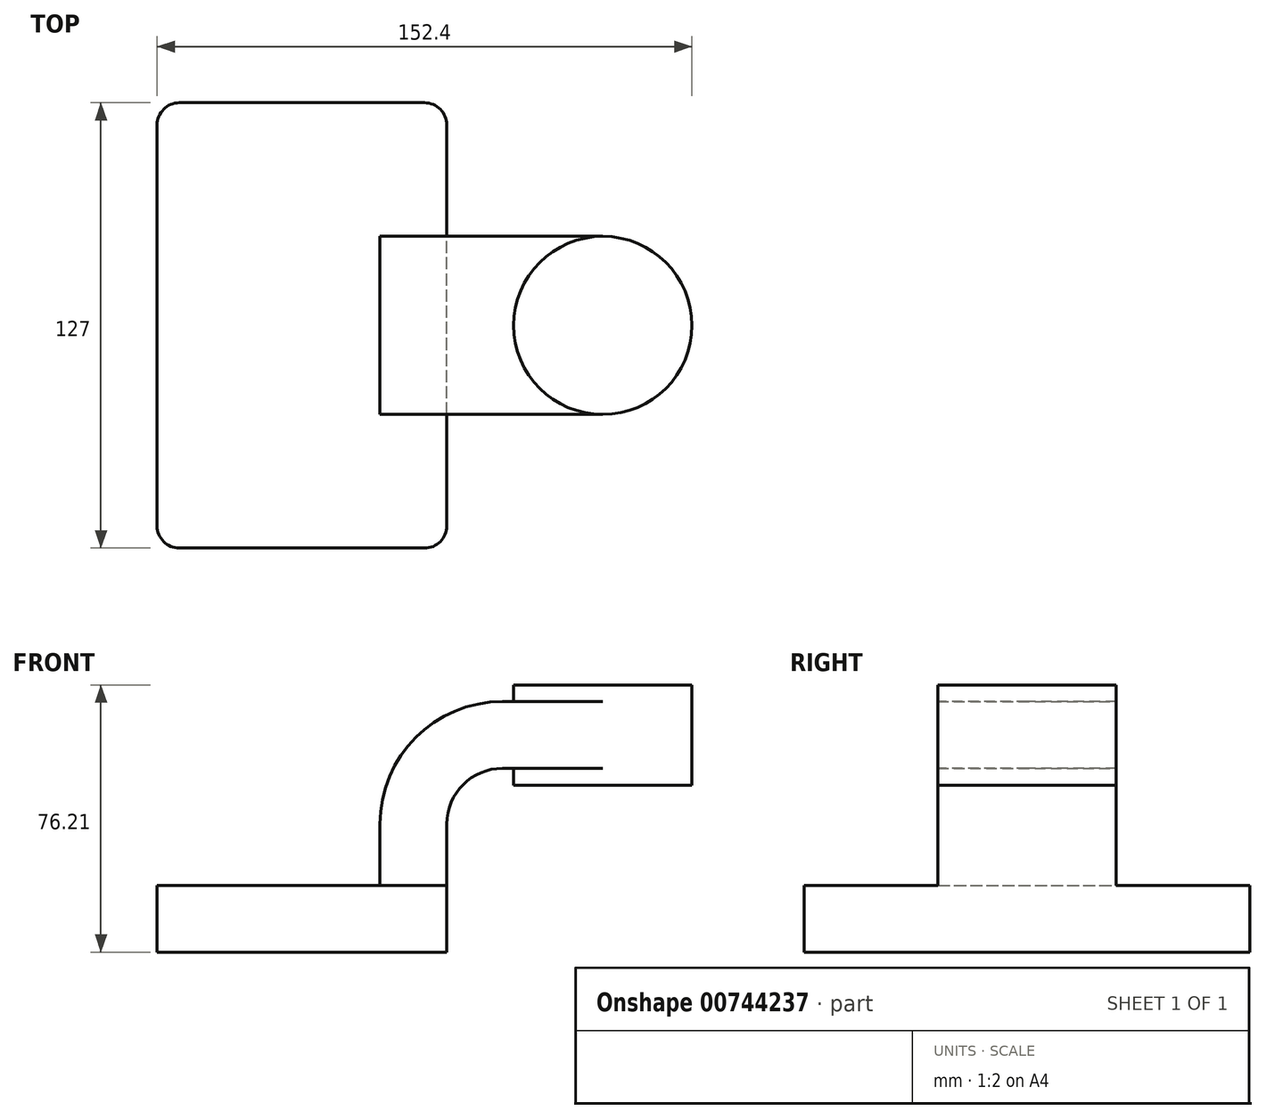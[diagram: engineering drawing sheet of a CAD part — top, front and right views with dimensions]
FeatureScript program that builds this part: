
annotation { "Feature Type Name" : "Feature", "Feature Type Description" : "" }
export const myFeature = defineFeature(function(context is Context, id is Id, definition is map)
    precondition{}
    {
        {
            var Q0;
            Q0=qCreatedBy(makeId("Front.planeOp"),FACE);
            var sketch = newSketch(context, id + "F0", { "sketchPlane" : qUnion([Q0])});
            skLineSegment(sketch, "E0.bottom", {"start": v(-41.27, -9.53) * mm, "end": v(41.28, -9.53) * mm});
            skLineSegment(sketch, "E0.top", {"start": v(-41.28, 9.53) * mm, "end": v(41.28, 9.53) * mm});
            skLineSegment(sketch, "E0.left", {"start": v(-41.28, -9.53) * mm, "end": v(-41.28, 9.53) * mm});
            skLineSegment(sketch, "E0.right", {"start": v(41.28, -9.53) * mm, "end": v(41.28, 9.53) * mm});
            skPoint(sketch, "E0.middle", {"position": v(0, 0) * mm});
            skLineSegment(sketch, "E1.bottom", {"start": v(60.33, 38.1) * mm, "end": v(111.12, 38.1) * mm});
            skLineSegment(sketch, "E1.top", {"start": v(60.33, 66.67) * mm, "end": v(111.12, 66.67) * mm});
            skLineSegment(sketch, "E1.left", {"start": v(60.33, 38.1) * mm, "end": v(60.33, 66.67) * mm});
            skLineSegment(sketch, "E1.right", {"start": v(111.12, 38.1) * mm, "end": v(111.12, 66.67) * mm});
            skPoint(sketch, "E1.middle", {"position": v(85.72, 52.39) * mm});
            skLineSegment(sketch, "E2", {"start": v(41.27, 9.52) * mm, "end": v(41.27, 27) * mm});
            skArc(sketch, "E3", {"start": v(41.27, 27) * mm, "mid": v(45.92, 38.23) * mm, "end": v(57.15, 42.88) * mm});
            skLineSegment(sketch, "E4", {"start": v(57.15, 42.88) * mm, "end": v(85.73, 42.88) * mm});
            skLineSegment(sketch, "E5.0", {"start": v(57.15, 61.93) * mm, "end": v(85.73, 61.93) * mm});
            skArc(sketch, "E5.1", {"start": v(22.23, 27) * mm, "mid": v(32.45, 51.7) * mm, "end": v(57.15, 61.93) * mm});
            skLineSegment(sketch, "E5.2", {"start": v(22.22, 9.52) * mm, "end": v(22.22, 27) * mm});
            skFitSpline(sketch, "E6", {"points": [v(-41.28, 9.53) * mm, v(57.15, 61.93) * mm], "startDerivative": vector(24.71, 99.66) * mm, "endDerivative": vector(155.21, -11.9) * mm});
            skLineSegment(sketch, "E7", {"start": v(85.72, 38.1) * mm, "end": v(85.72, 66.67) * mm});
            skSolve(sketch);
        }
        {
            var Q0;
            Q0=makeQuery(id+"F0.imprint","IMPRINT",FACE,{"disambiguationData":[TD([[makeQuery(id+"F0.imprint","IMPRINT",EDGE,{"derivedFrom":sQuery(id+"F0.wireOp",EDGE,"E0.bottom")}),1.0]])]});
            extrude(context, id + "F1", {"entities" : qUnion([Q0]), "endBound" : BoundingType.SYMMETRIC, "depth" : 127 * mm, "offsetDistance" : 25.4 * mm});
        }
        {
            var Q0;
            {var subQ0=sQuery(id+"F0.wireOp",EDGE,"E2");Q0=makeQuery(id+"F0.imprint","IMPRINT",FACE,{"disambiguationData":[TD([[makeQuery(id+"F0.imprint","IMPRINT",EDGE,{"derivedFrom":subQ0}),1.0]])]});}
            var Q1;
            {var subQ5=sQuery(id+"F0.wireOp",EDGE,"0U7YWErx-1dxw-9Tui-l4bp-ggx3hihpv42R");Q1=makeQuery(id+"F0.imprint","IMPRINT",FACE,{"disambiguationData":[TD([[makeQuery(id+"F0.imprint","IMPRINT",EDGE,{"derivedFrom":subQ5}),-1.0]])]});}
            var Q2;
            {var subQ0=sQuery(id+"F0.wireOp",EDGE,"E4");var subQ1=sQuery(id+"F0.wireOp",EDGE,"E1.left");var subQ2=makeQuery(id+"F0.imprint","INTERSECT",VERTEX,{"derivedFrom":[subQ1,subQ0]});Q2=makeQuery(id+"F0.imprint","IMPRINT",FACE,{"disambiguationData":[TD([[makeQuery(id+"F0.imprint","IMPRINT",EDGE,{"disambiguationData":[TD([[subQ2,-1.0]])],"derivedFrom":subQ1}),-1.0]])]});}
            extrude(context, id + "F2", {"entities" : qUnion([Q0, Q1, Q2]), "operationType" : NewBodyOperationType.ADD, "endBound" : BoundingType.SYMMETRIC, "depth" : 50.8 * mm, "offsetDistance" : 25.4 * mm});
        }
        {
            var Q0;
            Q0=makeQuery(id+"F0.imprint","IMPRINT",FACE,{"disambiguationData":[TD([[makeQuery(id+"F0.imprint","IMPRINT",EDGE,{"derivedFrom":sQuery(id+"F0.wireOp",EDGE,"E5.1")}),1.0]])]});
            extrude(context, id + "F3", {"entities" : qUnion([Q0]), "operationType" : NewBodyOperationType.ADD, "endBound" : BoundingType.SYMMETRIC, "depth" : 15.88 * mm, "offsetDistance" : 25.4 * mm});
        }
        {
            var Q0;
            {var subQ4=sQuery(id+"F0.wireOp",EDGE,"E1.right");Q0=makeQuery(id+"F0.imprint","IMPRINT",FACE,{"disambiguationData":[TD([[makeQuery(id+"F0.imprint","IMPRINT",EDGE,{"derivedFrom":subQ4}),1.0]])]});}
            var Q1;
            Q1=sQuery(id+"F0.wireOp",EDGE,"E7");
            revolve(context, id + "F4", {"operationType" : NewBodyOperationType.ADD, "surfaceOperationType" : NewSurfaceOperationType.NEW, "entities" : qUnion([Q0]), "axis" : qUnion([Q1]), "revolveType" : RevolveType.FULL});
        }
        {
            var Q0;
            Q0=makeQuery(id+"F1.opExtrude","CAP_EDGE",EDGE,{"disambiguationData":[OSD([sQuery(id+"F0.wireOp",EDGE,"E0.right")])],"isStart":false});
            var Q1;
            Q1=makeQuery(id+"F1.opExtrude","CAP_EDGE",EDGE,{"disambiguationData":[OSD([sQuery(id+"F0.wireOp",EDGE,"E0.left")])],"isStart":false});
            var Q2;
            Q2=makeQuery(id+"F1.opExtrude","CAP_EDGE",EDGE,{"disambiguationData":[OSD([sQuery(id+"F0.wireOp",EDGE,"E0.right")])],"isStart":true});
            var Q3;
            Q3=makeQuery(id+"F1.opExtrude","CAP_EDGE",EDGE,{"disambiguationData":[OSD([sQuery(id+"F0.wireOp",EDGE,"E0.left")])],"isStart":true});
            fillet(context, id + "F5", {"entities" : qUnion([Q0, Q1, Q2, Q3]), "radius" : 6.35 * mm, "tangentPropagation" : true, "allowEdgeOverflow" : false});
        }
    });
